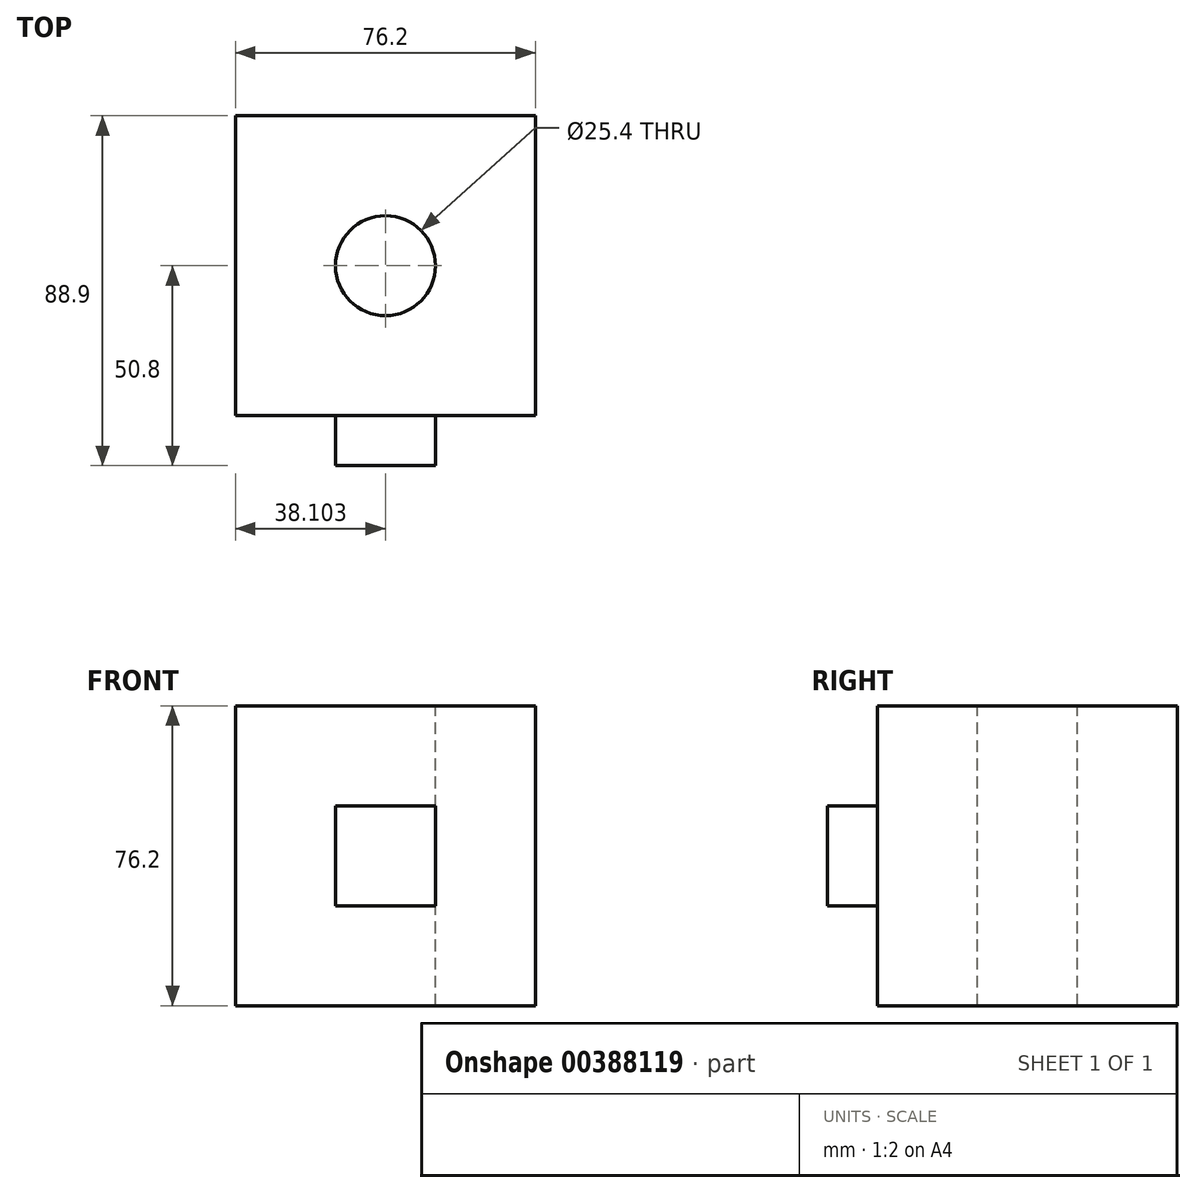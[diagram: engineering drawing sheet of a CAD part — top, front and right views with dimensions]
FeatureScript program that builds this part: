
annotation { "Feature Type Name" : "Feature", "Feature Type Description" : "" }
export const myFeature = defineFeature(function(context is Context, id is Id, definition is map)
    precondition{}
    {
        {
            var Q0;
            Q0=qCreatedBy(makeId("Front.planeOp"),FACE);
            var sketch = newSketch(context, id + "F0", { "sketchPlane" : qUnion([Q0])});
            skLineSegment(sketch, "E0.bottom", {"start": v(-31.72, 38.82) * mm, "end": v(44.48, 38.82) * mm});
            skLineSegment(sketch, "E0.top", {"start": v(-31.72, -37.38) * mm, "end": v(44.48, -37.38) * mm});
            skLineSegment(sketch, "E0.left", {"start": v(-31.72, 38.82) * mm, "end": v(-31.72, -37.38) * mm});
            skLineSegment(sketch, "E0.right", {"start": v(44.48, 38.82) * mm, "end": v(44.48, -37.38) * mm});
            skSolve(sketch);
        }
        {
            var Q0;
            Q0=makeQuery(id+"F0.imprint","IMPRINT",FACE,{"disambiguationData":[TD([[makeQuery(id+"F0.imprint","IMPRINT",EDGE,{"derivedFrom":sQuery(id+"F0.wireOp",EDGE,"E0.bottom")}),-1.0]])]});
            extrude(context, id + "F1", {"entities" : qUnion([Q0]), "depth" : 76.2 * mm});
        }
        {
            var Q0;
            Q0=makeQuery(id+"F1.opExtrude","SWEPT_FACE",FACE,{"disambiguationData":[OSD([sQuery(id+"F0.wireOp",EDGE,"E0.bottom")])]});
            var sketch = newSketch(context, id + "F2", { "sketchPlane" : qUnion([Q0])});
            skPoint(sketch, "E1", {"position": v(6.38, -38.1) * mm});
            skSolve(sketch);
        }
        {
            var Q0;
            Q0=sQuery(id+"F2.wireOp",VERTEX,"E1");
            var Q1;
            Q1=makeQuery(id+"F1.opExtrude","SWEPT_BODY",BODY,{"disambiguationData":[OSD([sQuery(id+"F0.wireOp",EDGE,"E0.bottom"),sQuery(id+"F0.wireOp",EDGE,"E0.top"),sQuery(id+"F0.wireOp",EDGE,"E0.left"),sQuery(id+"F0.wireOp",EDGE,"E0.right")])]});
            hole(context, id + "F3", {"style" : HoleStyle.SIMPLE, "endStyle" : HoleEndStyle.THROUGH, "holeDiameter" : 25.4 * mm, "isTappedThrough" : true, "tappedDepth" : 12.7 * mm, "tapClearance" : 3, "locations" : qUnion([Q0]), "scope" : qUnion([Q1])});
        }
        {
            var Q0;
            Q0=makeQuery(id+"F1.opExtrude","CAP_FACE",FACE,{"disambiguationData":[OSD([sQuery(id+"F0.wireOp",EDGE,"E0.bottom"),sQuery(id+"F0.wireOp",EDGE,"E0.top"),sQuery(id+"F0.wireOp",EDGE,"E0.left"),sQuery(id+"F0.wireOp",EDGE,"E0.right")])],"isStart":false});
            var sketch = newSketch(context, id + "F4", { "sketchPlane" : qUnion([Q0])});
            skLineSegment(sketch, "E2.bottom", {"start": v(-6.32, 13.42) * mm, "end": v(19.08, 13.42) * mm});
            skLineSegment(sketch, "E2.top", {"start": v(-6.32, -11.98) * mm, "end": v(19.08, -11.98) * mm});
            skLineSegment(sketch, "E2.left", {"start": v(-6.32, 13.42) * mm, "end": v(-6.32, -11.98) * mm});
            skLineSegment(sketch, "E2.right", {"start": v(19.08, 13.42) * mm, "end": v(19.08, -11.98) * mm});
            skSolve(sketch);
        }
        {
            var Q0;
            Q0=makeQuery(id+"F4.imprint","IMPRINT",FACE,{"disambiguationData":[TD([[makeQuery(id+"F4.imprint","IMPRINT",EDGE,{"derivedFrom":sQuery(id+"F4.wireOp",EDGE,"E2.bottom")}),-1.0]])]});
            extrude(context, id + "F5", {"entities" : qUnion([Q0]), "operationType" : NewBodyOperationType.ADD, "depth" : 12.7 * mm});
        }
    });
